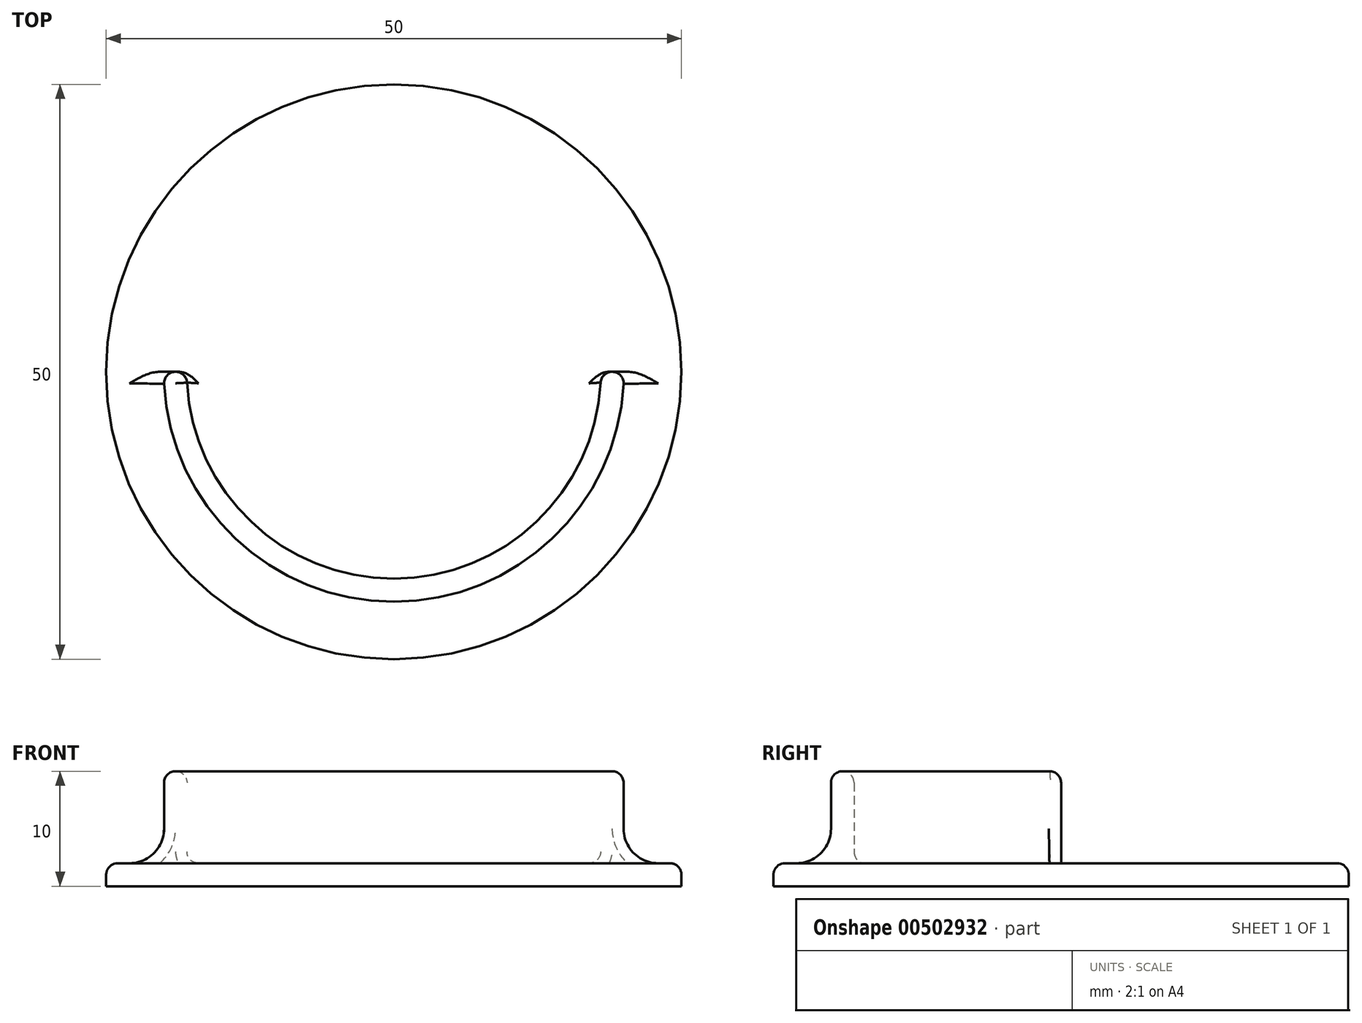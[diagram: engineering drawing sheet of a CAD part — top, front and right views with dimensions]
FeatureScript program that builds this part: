
annotation { "Feature Type Name" : "Feature", "Feature Type Description" : "" }
export const myFeature = defineFeature(function(context is Context, id is Id, definition is map)
    precondition{}
    {
        {
            var Q0;
            Q0=qCreatedBy(makeId("Top.planeOp"),FACE);
            var sketch = newSketch(context, id + "F0", { "sketchPlane" : qUnion([Q0])});
            skCircle(sketch, "E0", {"center": v(0, 0) * mm, "radius": 25 * mm});
            skCircle(sketch, "E1", {"center": v(0, 0) * mm, "radius": 20 * mm});
            skSolve(sketch);
        }
        {
            var Q0;
            Q0=qCreatedBy(makeId("Front.planeOp"),FACE);
            var sketch = newSketch(context, id + "F1", { "sketchPlane" : qUnion([Q0])});
            skLineSegment(sketch, "E2.bottom", {"start": v(-21, 2) * mm, "end": v(21, 2) * mm});
            skLineSegment(sketch, "E2.top", {"start": v(-21, 27.21) * mm, "end": v(21, 27.21) * mm});
            skLineSegment(sketch, "E2.left", {"start": v(-21, 2) * mm, "end": v(-21, 27.21) * mm});
            skLineSegment(sketch, "E2.right", {"start": v(21, 2) * mm, "end": v(21, 27.21) * mm});
            skSolve(sketch);
        }
        {
            var Q0;
            Q0=makeQuery(id+"F0.imprint","IMPRINT",FACE,{"disambiguationData":[TD([[makeQuery(id+"F0.imprint","IMPRINT",EDGE,{"derivedFrom":sQuery(id+"F0.wireOp",EDGE,"E0")}),1.0]])]});
            var Q1;
            Q1=makeQuery(id+"F0.imprint","IMPRINT",FACE,{"disambiguationData":[TD([[makeQuery(id+"F0.imprint","IMPRINT",EDGE,{"derivedFrom":sQuery(id+"F0.wireOp",EDGE,"E1")}),1.0]])]});
            extrude(context, id + "F2", {"entities" : qUnion([Q0, Q1]), "depth" : 2 * mm});
        }
        {
            var Q0;
            Q0=makeQuery(id+"F0.imprint","IMPRINT",FACE,{"disambiguationData":[TD([[makeQuery(id+"F0.imprint","IMPRINT",EDGE,{"derivedFrom":sQuery(id+"F0.wireOp",EDGE,"E1")}),1.0]])]});
            extrude(context, id + "F3", {"entities" : qUnion([Q0]), "operationType" : NewBodyOperationType.ADD, "depth" : 10 * mm});
        }
        {
            var Q0;
            Q0=makeQuery(id+"F3.opExtrude","CAP_FACE",FACE,{"disambiguationData":[OSD([sQuery(id+"F0.wireOp",EDGE,"E1")])],"isStart":false});
            shell(context, id + "F4", {"entities" : qUnion([Q0]), "thickness" : 2 * mm});
        }
        {
            var Q0;
            Q0=makeQuery(id+"F1.imprint","IMPRINT",FACE,{"disambiguationData":[TD([[makeQuery(id+"F1.imprint","IMPRINT",EDGE,{"derivedFrom":sQuery(id+"F1.wireOp",EDGE,"E2.bottom")}),1.0]])]});
            extrude(context, id + "F5", {"entities" : qUnion([Q0]), "operationType" : NewBodyOperationType.REMOVE, "oppositeDirection" : true, "depth" : 25 * mm});
        }
        {
            var Q0;
            Q0=makeQuery(id+"F4.opShell","TWEAK_EDGE",EDGE,{"derivedFrom":[makeQuery(id+"F2.opExtrude","CAP_FACE",FACE,{"disambiguationData":[OSD([sQuery(id+"F0.wireOp",EDGE,"E0")])],"isStart":true}),makeQuery(id+"F3.opExtrude","SWEPT_FACE",FACE,{"disambiguationData":[OSD([sQuery(id+"F0.wireOp",EDGE,"E1")])]})]});
            fillet(context, id + "F6", {"entities" : qUnion([Q0]), "radius" : 1 * mm, "tangentPropagation" : true, "allowEdgeOverflow" : false});
        }
        {
            var Q0;
            Q0=makeQuery(id+"F3.boolean.opBoolean","INTERSECT",EDGE,{"derivedFrom":[makeQuery(id+"F2.opExtrude","CAP_FACE",FACE,{"disambiguationData":[OSD([sQuery(id+"F0.wireOp",EDGE,"E0")])],"isStart":false}),makeQuery(id+"F3.opExtrude","SWEPT_FACE",FACE,{"disambiguationData":[OSD([sQuery(id+"F0.wireOp",EDGE,"E1")])]})]});
            fillet(context, id + "F7", {"entities" : qUnion([Q0]), "radius" : 3 * mm, "tangentPropagation" : true, "allowEdgeOverflow" : false});
        }
        {
            var Q0;
            Q0=makeQuery(id+"F3.opExtrude","CAP_EDGE",EDGE,{"disambiguationData":[OSD([sQuery(id+"F0.wireOp",EDGE,"E1")])],"isStart":false});
            var Q1;
            Q1=makeQuery(id+"F4.opShell","OFFSET_EDGE",EDGE,{"disambiguationData":[OSD([sQuery(id+"F0.wireOp",EDGE,"E1")])]});
            var Q2;
            Q2=makeQuery(id+"F5.boolean.opBoolean","INTERSECT",EDGE,{"disambiguationData":[OD(0.0)],"derivedFrom":[makeQuery(id+"F4.opShell","OFFSET_FACE",FACE,{"disambiguationData":[OSD([sQuery(id+"F0.wireOp",EDGE,"E1")])]}),makeQuery(id+"F5.opExtrude","CAP_FACE",FACE,{"disambiguationData":[OSD([sQuery(id+"F1.wireOp",EDGE,"E2.bottom"),sQuery(id+"F1.wireOp",EDGE,"E2.top"),sQuery(id+"F1.wireOp",EDGE,"E2.left"),sQuery(id+"F1.wireOp",EDGE,"E2.right")])],"isStart":true})]});
            var Q3;
            Q3=makeQuery(id+"F5.boolean.opBoolean","INTERSECT",EDGE,{"disambiguationData":[OD(1.0)],"derivedFrom":[makeQuery(id+"F4.opShell","OFFSET_FACE",FACE,{"disambiguationData":[OSD([sQuery(id+"F0.wireOp",EDGE,"E1")])]}),makeQuery(id+"F5.opExtrude","CAP_FACE",FACE,{"disambiguationData":[OSD([sQuery(id+"F1.wireOp",EDGE,"E2.bottom"),sQuery(id+"F1.wireOp",EDGE,"E2.top"),sQuery(id+"F1.wireOp",EDGE,"E2.left"),sQuery(id+"F1.wireOp",EDGE,"E2.right")])],"isStart":true})]});
            var Q4;
            Q4=makeQuery(id+"F5.boolean.opBoolean","INTERSECT",EDGE,{"disambiguationData":[OD(1.0)],"derivedFrom":[makeQuery(id+"F3.opExtrude","CAP_FACE",FACE,{"disambiguationData":[OSD([sQuery(id+"F0.wireOp",EDGE,"E1")])],"isStart":false}),makeQuery(id+"F5.opExtrude","CAP_FACE",FACE,{"disambiguationData":[OSD([sQuery(id+"F1.wireOp",EDGE,"E2.bottom"),sQuery(id+"F1.wireOp",EDGE,"E2.top"),sQuery(id+"F1.wireOp",EDGE,"E2.left"),sQuery(id+"F1.wireOp",EDGE,"E2.right")])],"isStart":true})]});
            var Q5;
            Q5=makeQuery(id+"F5.boolean.opBoolean","INTERSECT",EDGE,{"disambiguationData":[OD(1.0)],"derivedFrom":[makeQuery(id+"F3.opExtrude","SWEPT_FACE",FACE,{"disambiguationData":[OSD([sQuery(id+"F0.wireOp",EDGE,"E1")])]}),makeQuery(id+"F5.opExtrude","CAP_FACE",FACE,{"disambiguationData":[OSD([sQuery(id+"F1.wireOp",EDGE,"E2.bottom"),sQuery(id+"F1.wireOp",EDGE,"E2.top"),sQuery(id+"F1.wireOp",EDGE,"E2.left"),sQuery(id+"F1.wireOp",EDGE,"E2.right")])],"isStart":true})]});
            var Q6;
            Q6=makeQuery(id+"F5.boolean.opBoolean","INTERSECT",EDGE,{"disambiguationData":[OD(0.0)],"derivedFrom":[makeQuery(id+"F3.opExtrude","CAP_FACE",FACE,{"disambiguationData":[OSD([sQuery(id+"F0.wireOp",EDGE,"E1")])],"isStart":false}),makeQuery(id+"F5.opExtrude","CAP_FACE",FACE,{"disambiguationData":[OSD([sQuery(id+"F1.wireOp",EDGE,"E2.bottom"),sQuery(id+"F1.wireOp",EDGE,"E2.top"),sQuery(id+"F1.wireOp",EDGE,"E2.left"),sQuery(id+"F1.wireOp",EDGE,"E2.right")])],"isStart":true})]});
            var Q7;
            Q7=makeQuery(id+"F5.boolean.opBoolean","INTERSECT",EDGE,{"disambiguationData":[OD(0.0)],"derivedFrom":[makeQuery(id+"F3.opExtrude","SWEPT_FACE",FACE,{"disambiguationData":[OSD([sQuery(id+"F0.wireOp",EDGE,"E1")])]}),makeQuery(id+"F5.opExtrude","CAP_FACE",FACE,{"disambiguationData":[OSD([sQuery(id+"F1.wireOp",EDGE,"E2.bottom"),sQuery(id+"F1.wireOp",EDGE,"E2.top"),sQuery(id+"F1.wireOp",EDGE,"E2.left"),sQuery(id+"F1.wireOp",EDGE,"E2.right")])],"isStart":true})]});
            fillet(context, id + "F8", {"entities" : qUnion([Q0, Q1, Q2, Q3, Q4, Q5, Q6, Q7]), "radius" : 1 * mm, "tangentPropagation" : true, "allowEdgeOverflow" : false});
        }
        {
            var Q0;
            Q0=makeQuery(id+"F2.opExtrude","CAP_EDGE",EDGE,{"disambiguationData":[OSD([sQuery(id+"F0.wireOp",EDGE,"E0")])],"isStart":false});
            fillet(context, id + "F9", {"entities" : qUnion([Q0]), "radius" : 1 * mm, "tangentPropagation" : true, "allowEdgeOverflow" : false});
        }
    });
